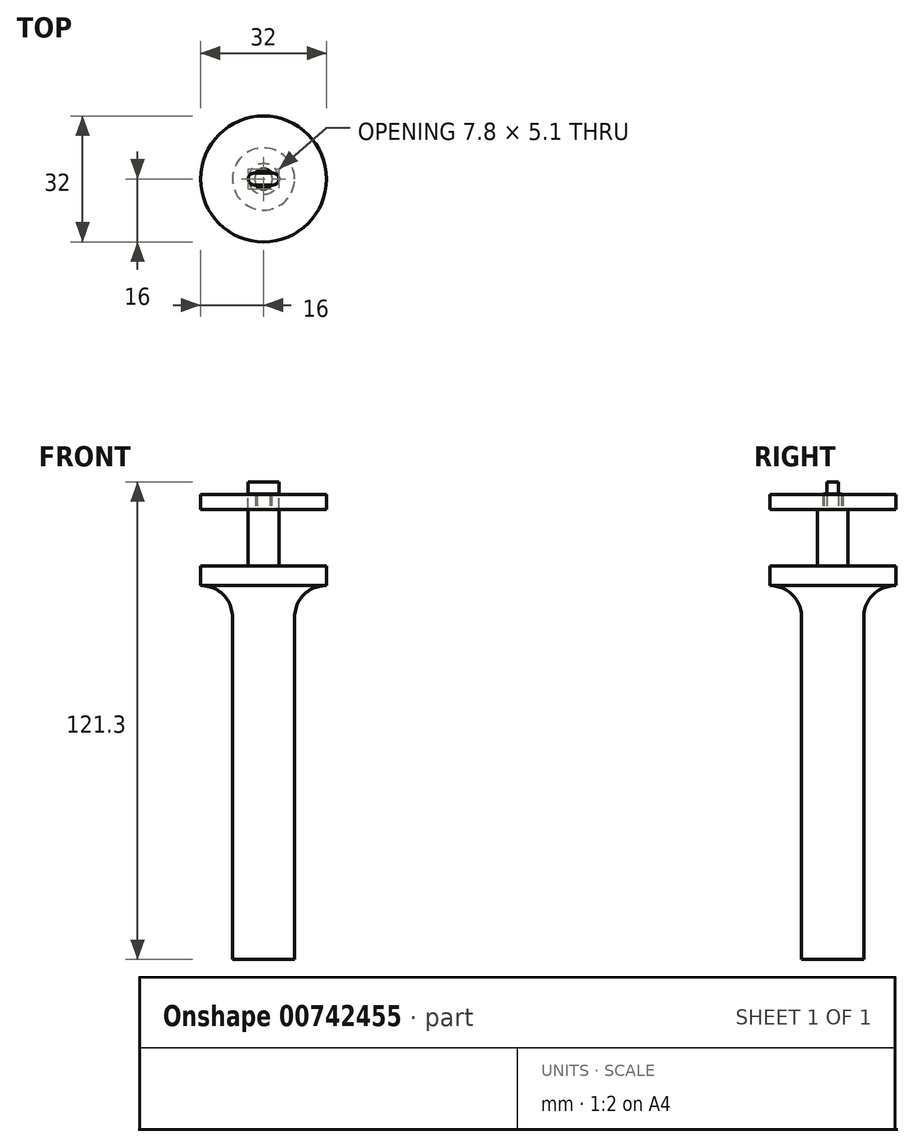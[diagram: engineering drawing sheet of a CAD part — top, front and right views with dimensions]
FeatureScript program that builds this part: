
annotation { "Feature Type Name" : "Feature", "Feature Type Description" : "" }
export const myFeature = defineFeature(function(context is Context, id is Id, definition is map)
    precondition{}
    {
        {
            var Q0;
            Q0=qCreatedBy(makeId("Top.planeOp"),FACE);
            var sketch = newSketch(context, id + "F0", { "sketchPlane" : qUnion([Q0])});
            skCircle(sketch, "E0", {"center": v(0, 0) * mm, "radius": 7.9 * mm});
            skSolve(sketch);
        }
        {
            var Q0;
            Q0 = qSketchRegion(id + "F0", true);
            extrude(context, id + "F1", {"entities" : qUnion([Q0]), "depth" : 100 * mm, "offsetDistance" : 25 * mm});
        }
        {
            var Q0;
            Q0=makeQuery(id+"F1.opExtrude","CAP_FACE",FACE,{"disambiguationData":[OSD([sQuery(id+"F0.wireOp",EDGE,"E0")])],"isStart":false});
            var sketch = newSketch(context, id + "F2", { "sketchPlane" : qUnion([Q0])});
            skCircle(sketch, "E1", {"center": v(0, 0) * mm, "radius": 3.9 * mm});
            skSolve(sketch);
        }
        {
            var Q0;
            Q0 = qSketchRegion(id + "F2", true);
            extrude(context, id + "F3", {"entities" : qUnion([Q0]), "operationType" : NewBodyOperationType.ADD, "depth" : 14.3 * mm, "offsetDistance" : 25 * mm});
        }
        {
            var Q0;
            Q0=makeQuery(id+"F3.opExtrude","CAP_FACE",FACE,{"disambiguationData":[OSD([sQuery(id+"F2.wireOp",EDGE,"E1")])],"isStart":false});
            var sketch = newSketch(context, id + "F4", { "sketchPlane" : qUnion([Q0])});
            skCircle(sketch, "E2", {"center": v(0, 0) * mm, "radius": 2.25 * mm});
            skSolve(sketch);
        }
        {
            var Q0;
            Q0 = qSketchRegion(id + "F4", true);
            extrude(context, id + "F5", {"entities" : qUnion([Q0]), "operationType" : NewBodyOperationType.ADD, "depth" : 4 * mm, "offsetDistance" : 25 * mm});
        }
        {
            var Q0;
            Q0=makeQuery(id+"F5.opExtrude","CAP_FACE",FACE,{"disambiguationData":[OSD([sQuery(id+"F4.wireOp",EDGE,"E2")])],"isStart":false});
            var sketch = newSketch(context, id + "F6", { "sketchPlane" : qUnion([Q0])});
            skLineSegment(sketch, "E3", {"start": v(0, 0) * mm, "end": v(3.9, 0) * mm, "construction": true});
            skLineSegment(sketch, "E4", {"start": v(0, 0) * mm, "end": v(-3.9, 0) * mm, "construction": true});
            skPoint(sketch, "E5", {"position": v(-2.4, 0) * mm});
            skPoint(sketch, "E6", {"position": v(2.4, 0) * mm});
            skLineSegment(sketch, "E7", {"start": v(-2.4, 0) * mm, "end": v(-2.4, 1.5) * mm, "construction": true});
            skLineSegment(sketch, "E8", {"start": v(-2.4, 0) * mm, "end": v(-2.4, -1.5) * mm, "construction": true});
            skArc(sketch, "E9", {"start": v(-2.4, -1.5) * mm, "mid": v(-3.9, 0) * mm, "end": v(-2.4, 1.5) * mm});
            skArc(sketch, "E10.MirrorCS", {"start": v(2.4, -1.5) * mm, "mid": v(3.9, 0) * mm, "end": v(2.4, 1.5) * mm});
            skLineSegment(sketch, "E11", {"start": v(2.4, 1.5) * mm, "end": v(-2.4, 1.5) * mm});
            skLineSegment(sketch, "E12", {"start": v(-2.4, -1.5) * mm, "end": v(2.4, -1.5) * mm});
            skSolve(sketch);
        }
        {
            var Q0;
            Q0 = qSketchRegion(id + "F6", true);
            extrude(context, id + "F7", {"entities" : qUnion([Q0]), "operationType" : NewBodyOperationType.ADD, "depth" : 3 * mm, "offsetDistance" : 25 * mm});
        }
        {
            var Q0;
            Q0=makeQuery(id+"F3.opExtrude","CAP_FACE",FACE,{"disambiguationData":[OSD([sQuery(id+"F2.wireOp",EDGE,"E1")])],"isStart":false});
            var sketch = newSketch(context, id + "F8", { "sketchPlane" : qUnion([Q0])});
            skCircle(sketch, "E13", {"center": v(0, 0) * mm, "radius": 2.55 * mm});
            skCircle(sketch, "E14", {"center": v(0, 0) * mm, "radius": 16 * mm});
            skSolve(sketch);
        }
        {
            var Q0;
            Q0 = qSketchRegion(id + "F8", true);
            extrude(context, id + "F9", {"entities" : qUnion([Q0]), "depth" : 3.9 * mm, "offsetDistance" : 25 * mm});
        }
        {
            var Q0;
            Q0=makeQuery(id+"F9.opExtrude","CAP_FACE",FACE,{"disambiguationData":[OSD([sQuery(id+"F8.wireOp",EDGE,"E13"),sQuery(id+"F8.wireOp",EDGE,"E14")])],"isStart":false});
            var sketch = newSketch(context, id + "F10", { "sketchPlane" : qUnion([Q0])});
            skLineSegment(sketch, "E15", {"start": v(0, 0) * mm, "end": v(3.9, 0) * mm, "construction": true});
            skLineSegment(sketch, "E16", {"start": v(0, 0) * mm, "end": v(-3.9, 0) * mm, "construction": true});
            skPoint(sketch, "E17", {"position": v(-2.4, 0) * mm});
            skPoint(sketch, "E18", {"position": v(2.4, 0) * mm});
            skLineSegment(sketch, "E19", {"start": v(-2.4, 0) * mm, "end": v(-2.4, 1.5) * mm, "construction": true});
            skLineSegment(sketch, "E20", {"start": v(2.4, 0) * mm, "end": v(2.4, 1.5) * mm, "construction": true});
            skArc(sketch, "E21", {"start": v(-2.4, 1.5) * mm, "mid": v(-3.9, 0) * mm, "end": v(-2.4, -1.5) * mm});
            skArc(sketch, "E22", {"start": v(2.4, 1.5) * mm, "mid": v(3.9, 0) * mm, "end": v(2.4, -1.5) * mm});
            skLineSegment(sketch, "E23", {"start": v(2.4, 1.5) * mm, "end": v(-2.4, 1.5) * mm});
            skLineSegment(sketch, "E24", {"start": v(-2.4, -1.5) * mm, "end": v(2.4, -1.5) * mm});
            skSolve(sketch);
        }
        {
            var Q0;
            Q0 = qSketchRegion(id + "F10", true);
            var Q1;
            Q1=makeQuery(id+"F9.opExtrude","CAP_FACE",FACE,{"disambiguationData":[OSD([sQuery(id+"F8.wireOp",EDGE,"E13"),sQuery(id+"F8.wireOp",EDGE,"E14")])],"isStart":true});
            extrude(context, id + "F11", {"entities" : qUnion([Q0]), "operationType" : NewBodyOperationType.REMOVE, "endBound" : BoundingType.UP_TO_SURFACE, "oppositeDirection" : true, "depth" : 25 * mm, "endBoundEntityFace" : qUnion([Q1]), "offsetDistance" : 25 * mm});
        }
        {
            var Q0;
            Q0=makeQuery(id+"F1.opExtrude","CAP_FACE",FACE,{"disambiguationData":[OSD([sQuery(id+"F0.wireOp",EDGE,"E0")])],"isStart":false});
            var sketch = newSketch(context, id + "F12", { "sketchPlane" : qUnion([Q0])});
            skCircle(sketch, "E25", {"center": v(0, 0) * mm, "radius": 16 * mm});
            skSolve(sketch);
        }
        {
            var Q0;
            Q0 = qSketchRegion(id + "F12", true);
            extrude(context, id + "F13", {"entities" : qUnion([Q0]), "operationType" : NewBodyOperationType.ADD, "oppositeDirection" : true, "depth" : 5 * mm, "offsetDistance" : 25 * mm});
        }
        {
            var Q0;
            Q0=makeQuery(id+"F13.boolean.opBoolean","INTERSECT",EDGE,{"derivedFrom":[makeQuery(id+"F1.opExtrude","SWEPT_FACE",FACE,{"disambiguationData":[OSD([sQuery(id+"F0.wireOp",EDGE,"E0")])]}),makeQuery(id+"F13.opExtrude","CAP_FACE",FACE,{"disambiguationData":[OSD([sQuery(id+"F12.wireOp",EDGE,"E25")])],"isStart":false})]});
            fillet(context, id + "F14", {"entities" : qUnion([Q0]), "radius" : 8 * mm, "tangentPropagation" : true, "allowEdgeOverflow" : false});
        }
    });
